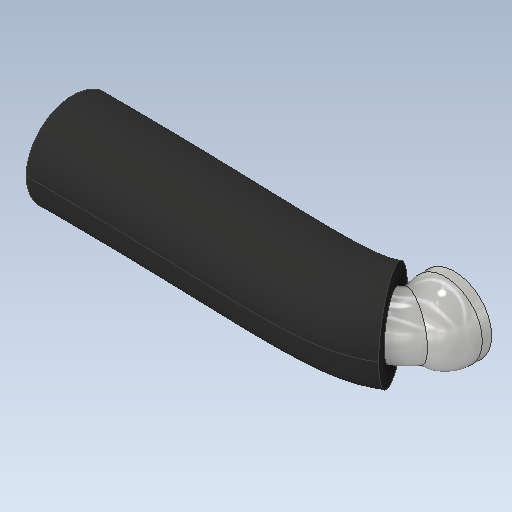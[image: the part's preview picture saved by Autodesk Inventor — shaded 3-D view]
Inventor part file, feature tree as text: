
AUTODESK INVENTOR PART (.ipt)
format: ipt  version: 2020.1 (Build 241239000, 239)  size: 237,568 bytes
history: native  units: mm
features: sketch x5, sweep x2, extrude x1, fillet x1, plane x1
ambient origin geometry x8: Origin, YZ Plane, XZ Plane, XY Plane, X Axis, Y Axis, Z Axis, Center Point
bodies: Solid1 (feature_tree)
feature tree (10):
  extrude  "Extrusion1"  Depth=2.5mm TaperAngle=0.0deg
  fillet  "Fillet1"  Radius=2.0mm
  sweep  "Sweep1"
  plane  "Work Plane1"
  sweep  "Sweep4"
  sketch  "Sketch1"  dims[d0=4.0mm d1=2.5mm d2=0.0mm d3=2.0mm]
  sketch  "Sketch2"  dims[d4=2.6mm d5=3.06mm]
  sketch  "Sketch3"  dims[d6=0.0mm d7=0.0mm d9=5.0mm]
  sketch  "Sketch4"  dims[d18=4.0mm d19=-2.0mm d20=0.0mm d21=0.0mm]
  sketch  "3D Sketch1"
